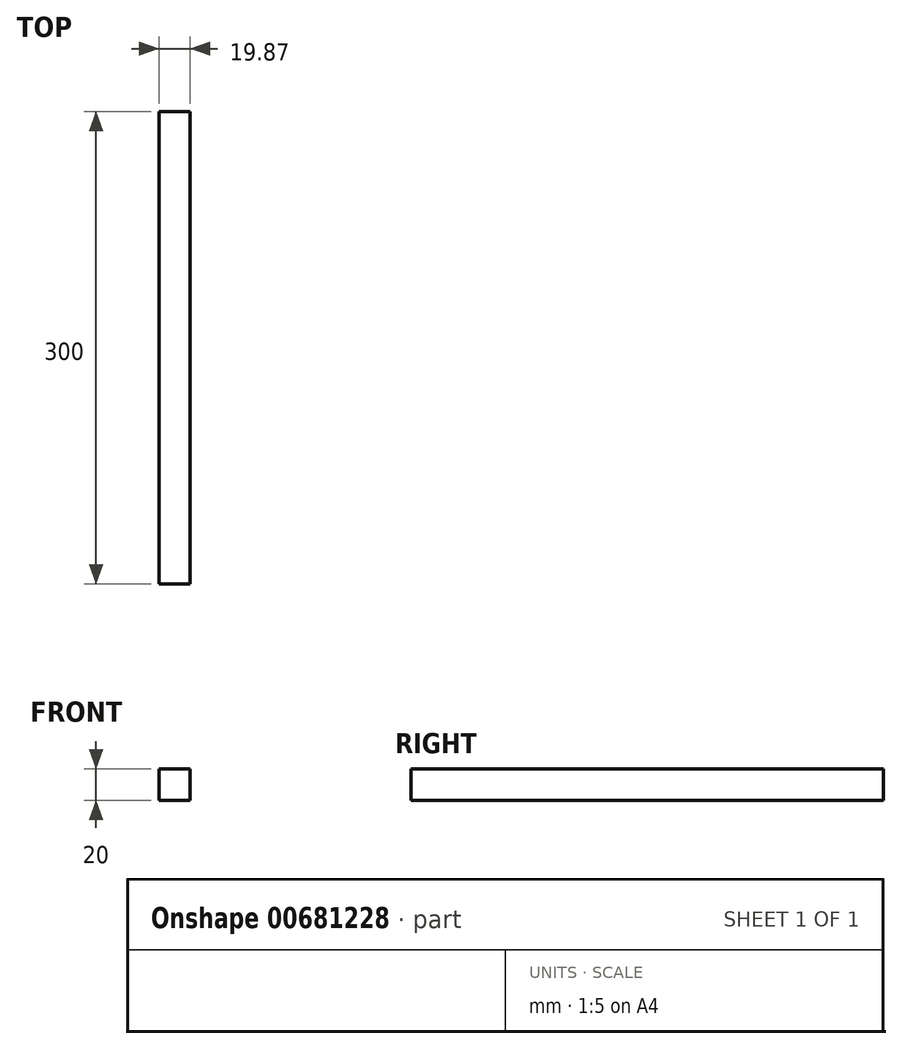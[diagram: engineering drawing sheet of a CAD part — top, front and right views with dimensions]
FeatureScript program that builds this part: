
annotation { "Feature Type Name" : "Feature", "Feature Type Description" : "" }
export const myFeature = defineFeature(function(context is Context, id is Id, definition is map)
    precondition{}
    {
        {
            var Q0;
            Q0=qCreatedBy(makeId("Front.planeOp"),FACE);
            var sketch = newSketch(context, id + "F0", { "sketchPlane" : qUnion([Q0])});
            skLineSegment(sketch, "E0", {"start": v(-19.75, 20) * mm, "end": v(0, 20) * mm});
            skLineSegment(sketch, "E1", {"start": v(0, 0) * mm, "end": v(-19.87, 0) * mm});
            skLineSegment(sketch, "E2", {"start": v(-19.87, 0) * mm, "end": v(-19.75, 20) * mm});
            skLineSegment(sketch, "E3", {"start": v(0, 20) * mm, "end": v(0, 0) * mm});
            skSolve(sketch);
        }
        {
            var Q0;
            Q0 = qSketchRegion(id + "F0", true);
            extrude(context, id + "F1", {"entities" : qUnion([Q0]), "depth" : 300 * mm, "offsetDistance" : 25 * mm});
        }
    });
